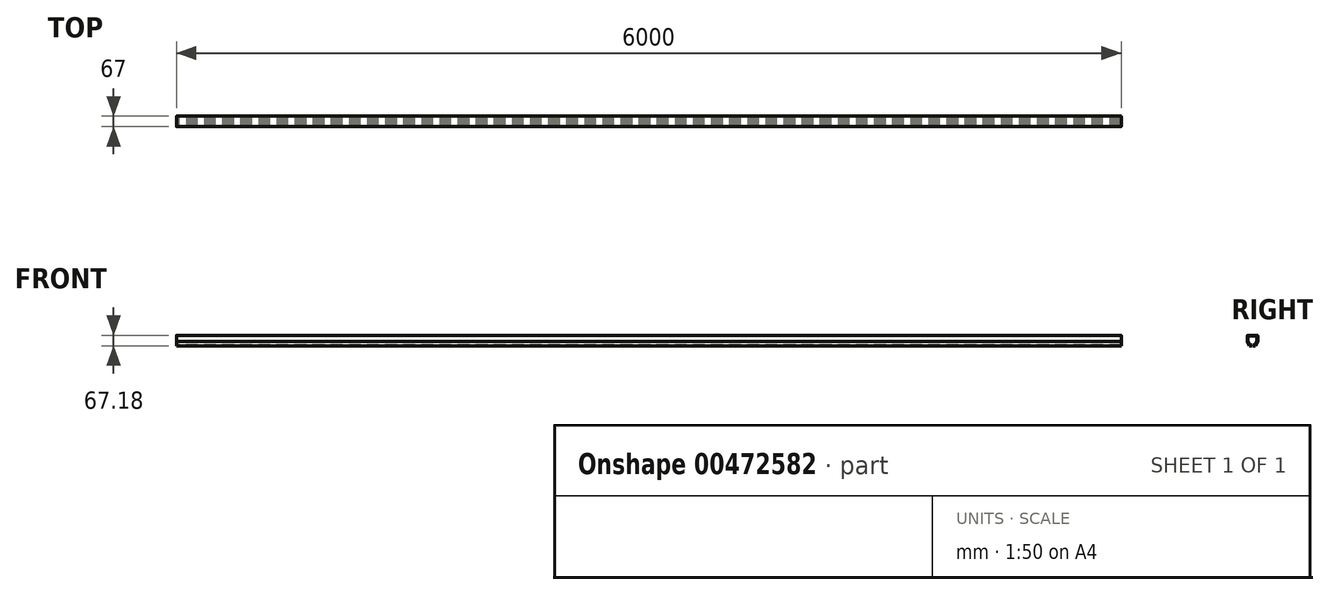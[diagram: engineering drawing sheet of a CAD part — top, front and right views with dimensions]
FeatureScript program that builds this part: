
annotation { "Feature Type Name" : "Feature", "Feature Type Description" : "" }
export const myFeature = defineFeature(function(context is Context, id is Id, definition is map)
    precondition{}
    {
        {
            var Q0;
            Q0=qCreatedBy(makeId("Right.planeOp"),FACE);
            var sketch = newSketch(context, id + "F0", { "sketchPlane" : qUnion([Q0])});
            skLineSegment(sketch, "E0", {"start": v(-45.34, 74.64) * mm, "end": v(-45.34, 114.64) * mm});
            skLineSegment(sketch, "E1", {"start": v(-45.34, 114.64) * mm, "end": v(21.66, 114.64) * mm});
            skLineSegment(sketch, "E2", {"start": v(21.66, 114.64) * mm, "end": v(21.66, 74.64) * mm});
            skLineSegment(sketch, "E3", {"start": v(-45.34, 74.64) * mm, "end": v(-30.95, 47.46) * mm});
            skLineSegment(sketch, "E4", {"start": v(-30.95, 47.46) * mm, "end": v(-15.08, 47.46) * mm});
            skLineSegment(sketch, "E5.MirrorCS", {"start": v(21.66, 74.64) * mm, "end": v(7.28, 47.46) * mm});
            skLineSegment(sketch, "E6.MirrorCS", {"start": v(7.28, 47.46) * mm, "end": v(-8.59, 47.46) * mm});
            skPoint(sketch, "E7.start.orphan", {"position": v(-11.84, 114.64) * mm});
            skLineSegment(sketch, "E8.0", {"start": v(4.27, 52.46) * mm, "end": v(-8.59, 52.46) * mm});
            skLineSegment(sketch, "E8.1", {"start": v(16.66, 75.88) * mm, "end": v(4.27, 52.46) * mm});
            skLineSegment(sketch, "E8.2", {"start": v(16.66, 109.64) * mm, "end": v(16.66, 75.88) * mm});
            skLineSegment(sketch, "E8.3", {"start": v(-27.94, 52.46) * mm, "end": v(-15.08, 52.46) * mm});
            skLineSegment(sketch, "E8.4", {"start": v(-40.34, 75.88) * mm, "end": v(-27.94, 52.46) * mm});
            skLineSegment(sketch, "E8.5", {"start": v(-40.34, 75.88) * mm, "end": v(-40.34, 109.64) * mm});
            skLineSegment(sketch, "E8.6", {"start": v(-40.34, 109.64) * mm, "end": v(16.66, 109.64) * mm});
            skLineSegment(sketch, "E9", {"start": v(-15.08, 52.46) * mm, "end": v(-15.08, 47.46) * mm});
            skLineSegment(sketch, "E10", {"start": v(-8.59, 52.46) * mm, "end": v(-8.59, 47.46) * mm});
            skSolve(sketch);
        }
        {
            var Q0;
            Q0=makeQuery(id+"F0.imprint","IMPRINT",FACE,{"disambiguationData":[TD([[makeQuery(id+"F0.imprint","IMPRINT",EDGE,{"derivedFrom":sQuery(id+"F0.wireOp",EDGE,"E0")}),-1.0]])]});
            extrude(context, id + "F1", {"entities" : qUnion([Q0]), "depth" : 6000 * mm});
        }
        {
            var Q0;
            Q0=makeQuery(id+"F1.opExtrude","SWEPT_EDGE",EDGE,{"disambiguationData":[OSD([sQuery(id+"F0.wireOp",EDGE,"E1"),sQuery(id+"F0.wireOp",EDGE,"E2")])]});
            var Q1;
            Q1=makeQuery(id+"F1.opExtrude","SWEPT_EDGE",EDGE,{"disambiguationData":[OSD([sQuery(id+"F0.wireOp",EDGE,"E0"),sQuery(id+"F0.wireOp",EDGE,"E1")])]});
            fillet(context, id + "F2", {"entities" : qUnion([Q0, Q1]), "radius" : 5 * mm, "tangentPropagation" : true, "allowEdgeOverflow" : false});
        }
    });
